# Revit family: XXXBasin-Wall_Hung-DXV-COSSU-D20040001.415
name_source: partatom
category: Plumbing Fixtures
units: mm (PartAtom-declared; Revit-internal decimal feet)

## family parameters
Cut with Voids When Loaded = No
Host = Face
OmniClass Number = 23.45.05.14.14
OmniClass Title = Sinks/Lavatories
Part Type = Normal
Room Calculation Point = No
Round Connector Dimension = Use Radius
Shared = Yes

## types (1)
- D20040001.415
    Assembly Code = D2010310
    Basin Shape = Eclipse Corner Sink
    Bowl Depth = 4 1/4"
    Bowl Width = 13 1/4"
    CW Connection = Yes
    CWFU = 1.5
    Cold Water Connection Diameter = 1/2"
    Cold Water Connection Height = 24"
    Cold Water Connection Radius = 1/4"
    Cold Water Connection Width = 6"
    Default Elevation = 34 1/2"
    Description = Cossu Small Wall-Hung Lavatory
    Finish = Fine Fire Clay-DXV-415-Canvas White
    HW Connection = Yes
    HWFU = 1.5
    Height = 5 9/16"
    Hot Water Connection Diameter = 1/2"
    Hot Water Connection Height = 24"
    Hot Water Connection Radius = 1/4"
    Hot Water Connection Width = 6"
    Installation Type = Corner Wall-Mounted
    Length = 17"
    Manufacturer = DXV
    Material = Fine Fire Clay-DXV-415-Canvas White
    Model = D20040001.415
    Price = Prices may vary. Please consult Manufacturer Representative for most up-to-date price list.
    Product Documentation Link = https://dxv01.blob.core.windows.net
    Product Page URL = https://www.dxv.com
    Revised Date = 11/15/2021
    URL = https://www.dxv.com
    Vent Connection = No
    WFU = 2
    Warranty Documentation Link = https://www.dxv.com
    Waste Connection = Yes
    Waste Connection Diameter = 1 1/4"
    Waste Connection Height = 22"
    Waste Connection Radius = 5/8"
    Waste Connection Width = 5"
    Width = 12"

## geometry (parser evidence)
native form markers: Sweep x3
no freeform markers — native parametric forms only
